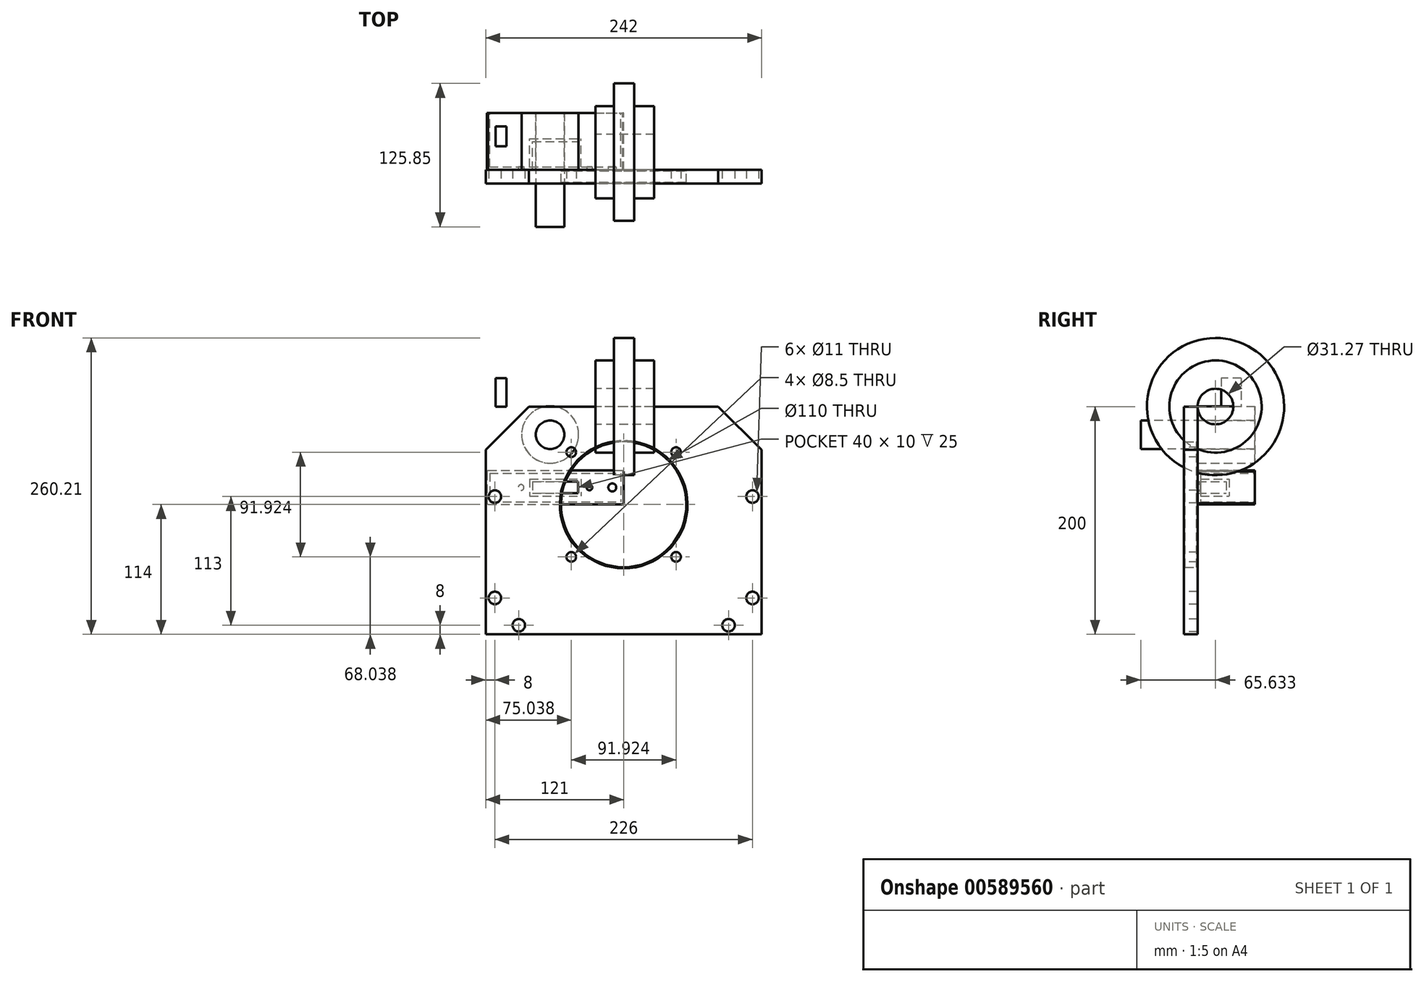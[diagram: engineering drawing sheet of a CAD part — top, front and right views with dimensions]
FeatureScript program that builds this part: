
annotation { "Feature Type Name" : "Feature", "Feature Type Description" : "" }
export const myFeature = defineFeature(function(context is Context, id is Id, definition is map)
    precondition{}
    {
        {
            var Q0;
            Q0=qCreatedBy(makeId("Front.planeOp"),FACE);
            var sketch = newSketch(context, id + "F0", { "sketchPlane" : qUnion([Q0])});
            skLineSegment(sketch, "E0.bottom", {"start": v(-120, 30) * mm, "end": v(0, 30) * mm});
            skLineSegment(sketch, "E0.top", {"start": v(-120, 0) * mm, "end": v(0, 0) * mm});
            skLineSegment(sketch, "E0.left", {"start": v(-120, 30) * mm, "end": v(-120, 0) * mm});
            skLineSegment(sketch, "E0.right", {"start": v(0, 30) * mm, "end": v(0, 0) * mm});
            skSolve(sketch);
        }
        {
            var Q0;
            Q0 = qSketchRegion(id + "F0", true);
            extrude(context, id + "F1", {"entities" : qUnion([Q0]), "depth" : 25 * mm, "offsetDistance" : 25 * mm});
        }
        {
            var Q0;
            Q0=makeQuery(id+"F1.opExtrude","CAP_FACE",FACE,{"disambiguationData":[OSD([sQuery(id+"F0.wireOp",EDGE,"E0.bottom"),sQuery(id+"F0.wireOp",EDGE,"E0.top"),sQuery(id+"F0.wireOp",EDGE,"E0.left"),sQuery(id+"F0.wireOp",EDGE,"E0.right")])],"isStart":false});
            var sketch = newSketch(context, id + "F2", { "sketchPlane" : qUnion([Q0])});
            skLineSegment(sketch, "E1.bottom", {"start": v(-80, 20) * mm, "end": v(-40, 20) * mm});
            skLineSegment(sketch, "E1.top", {"start": v(-80, 10) * mm, "end": v(-40, 10) * mm});
            skLineSegment(sketch, "E1.left", {"start": v(-80, 20) * mm, "end": v(-80, 10) * mm});
            skLineSegment(sketch, "E1.right", {"start": v(-40, 20) * mm, "end": v(-40, 10) * mm});
            skSolve(sketch);
        }
        {
            var Q0;
            Q0=makeQuery(id+"F2.imprint","IMPRINT",FACE,{"disambiguationData":[TD([[makeQuery(id+"F2.imprint","IMPRINT",EDGE,{"derivedFrom":sQuery(id+"F2.wireOp",EDGE,"E1.bottom")}),1.0]])]});
            extrude(context, id + "F3", {"entities" : qUnion([Q0]), "operationType" : NewBodyOperationType.ADD, "depth" : 25 * mm, "offsetDistance" : 25 * mm});
        }
        {
            var Q0;
            Q0=makeQuery(id+"F1.opExtrude","CAP_FACE",FACE,{"disambiguationData":[OSD([sQuery(id+"F0.wireOp",EDGE,"E0.bottom"),sQuery(id+"F0.wireOp",EDGE,"E0.top"),sQuery(id+"F0.wireOp",EDGE,"E0.left"),sQuery(id+"F0.wireOp",EDGE,"E0.right")])],"isStart":true});
            shell(context, id + "F4", {"entities" : qUnion([Q0]), "thickness" : 2.5 * mm});
        }
        {
            var Q0;
            Q0=makeQuery(id+"F3.opExtrude","CAP_FACE",FACE,{"disambiguationData":[OSD([sQuery(id+"F0.wireOp",EDGE,"E0.bottom"),sQuery(id+"F0.wireOp",EDGE,"E0.top"),sQuery(id+"F0.wireOp",EDGE,"E0.left"),sQuery(id+"F0.wireOp",EDGE,"E0.right"),sQuery(id+"F2.wireOp",EDGE,"E1.bottom"),sQuery(id+"F2.wireOp",EDGE,"E1.top"),sQuery(id+"F2.wireOp",EDGE,"E1.left"),sQuery(id+"F2.wireOp",EDGE,"E1.right")])],"isStart":false});
            var sketch = newSketch(context, id + "F5", { "sketchPlane" : qUnion([Q0])});
            skPoint(sketch, "E2", {"position": v(-90, 15) * mm});
            skPoint(sketch, "E3", {"position": v(-30, 15) * mm});
            skPoint(sketch, "E4", {"position": v(-10, 15) * mm});
            skSolve(sketch);
        }
        {
            var Q0;
            Q0=sQuery(id+"F5.wireOp",VERTEX,"E2");
            var Q1;
            Q1=sQuery(id+"F5.wireOp",VERTEX,"E3");
            var Q2;
            Q2=makeQuery(id+"F1.opExtrude","SWEPT_BODY",BODY,{"disambiguationData":[OSD([sQuery(id+"F0.wireOp",EDGE,"E0.bottom"),sQuery(id+"F0.wireOp",EDGE,"E0.top"),sQuery(id+"F0.wireOp",EDGE,"E0.left"),sQuery(id+"F0.wireOp",EDGE,"E0.right")])]});
            hole(context, id + "F6", {"style" : HoleStyle.SIMPLE, "endStyle" : HoleEndStyle.THROUGH, "holeDiameter" : 5 * mm, "majorDiameter" : 5 * mm, "isTappedThrough" : true, "tappedDepth" : 12 * mm, "tapClearance" : 3, "locations" : qUnion([Q0, Q1]), "scope" : qUnion([Q2])});
        }
        {
            var Q0;
            Q0=sQuery(id+"F5.wireOp",VERTEX,"E4");
            var Q1;
            Q1=makeQuery(id+"F1.opExtrude","SWEPT_BODY",BODY,{"disambiguationData":[OSD([sQuery(id+"F0.wireOp",EDGE,"E0.bottom"),sQuery(id+"F0.wireOp",EDGE,"E0.top"),sQuery(id+"F0.wireOp",EDGE,"E0.left"),sQuery(id+"F0.wireOp",EDGE,"E0.right")])]});
            hole(context, id + "F7", {"style" : HoleStyle.SIMPLE, "endStyle" : HoleEndStyle.THROUGH, "standardTappedOrClearance" : lookupTablePath({ "standard" : "ISO", "engagement" : "75%", "pitch" : "1 mm", "size" : "M8", "type" : "Tapped" }), "standardBlindInLast" : lookupTablePath({ "standard" : "ISO", "engagement" : "75%", "pitch" : "1 mm", "size" : "M8", "type" : "Tapped" }), "holeDiameter" : 7 * mm, "majorDiameter" : 8 * mm, "showTappedDepth" : true, "isTappedThrough" : true, "tappedDepth" : 12 * mm, "tapClearance" : 3, "locations" : qUnion([Q0]), "scope" : qUnion([Q1])});
        }
        {
            var Q0;
            {var subQ0=sQuery(id+"F0.wireOp",EDGE,"E0.left");var subQ1=sQuery(id+"F0.wireOp",EDGE,"E0.bottom");Q0=makeQuery(id+"F3.boolean.opBoolean","MERGE",EDGE,{"derivedFrom":[makeQuery(id+"F1.opExtrude","SWEPT_EDGE",EDGE,{"disambiguationData":[OSD([subQ1,subQ0])]}),makeQuery(id+"F3.opExtrude","SWEPT_EDGE",EDGE,{"disambiguationData":[OSD([subQ1,subQ0])]})]});}
            var Q1;
            {var subQ0=sQuery(id+"F0.wireOp",EDGE,"E0.left");var subQ1=sQuery(id+"F0.wireOp",EDGE,"E0.top");Q1=makeQuery(id+"F3.boolean.opBoolean","MERGE",EDGE,{"derivedFrom":[makeQuery(id+"F1.opExtrude","SWEPT_EDGE",EDGE,{"disambiguationData":[OSD([subQ1,subQ0])]}),makeQuery(id+"F3.opExtrude","SWEPT_EDGE",EDGE,{"disambiguationData":[OSD([subQ1,subQ0])]})]});}
            var Q2;
            {var subQ0=sQuery(id+"F0.wireOp",EDGE,"E0.right");var subQ1=sQuery(id+"F0.wireOp",EDGE,"E0.bottom");Q2=makeQuery(id+"F3.boolean.opBoolean","MERGE",EDGE,{"derivedFrom":[makeQuery(id+"F1.opExtrude","SWEPT_EDGE",EDGE,{"disambiguationData":[OSD([subQ1,subQ0])]}),makeQuery(id+"F3.opExtrude","SWEPT_EDGE",EDGE,{"disambiguationData":[OSD([subQ1,subQ0])]})]});}
            var Q3;
            {var subQ0=sQuery(id+"F0.wireOp",EDGE,"E0.right");var subQ1=sQuery(id+"F0.wireOp",EDGE,"E0.top");Q3=makeQuery(id+"F3.boolean.opBoolean","MERGE",EDGE,{"derivedFrom":[makeQuery(id+"F1.opExtrude","SWEPT_EDGE",EDGE,{"disambiguationData":[OSD([subQ1,subQ0])]}),makeQuery(id+"F3.opExtrude","SWEPT_EDGE",EDGE,{"disambiguationData":[OSD([subQ1,subQ0])]})]});}
            chamfer(context, id + "F8", {"entities" : qUnion([Q0, Q1, Q2, Q3]), "width" : 1 * mm, "tangentPropagation" : true});
        }
        {
            var Q0;
            Q0=qCreatedBy(makeId("Front.planeOp"),FACE);
            var sketch = newSketch(context, id + "F9", { "sketchPlane" : qUnion([Q0])});
            skCircle(sketch, "E5", {"center": v(-64.52, 61.3) * mm, "radius": 25 * mm});
            skCircle(sketch, "E6", {"center": v(-64.52, 61.3) * mm, "radius": 12.5 * mm});
            skSolve(sketch);
        }
        {
            var Q0;
            Q0=makeQuery(id+"F9.imprint","IMPRINT",FACE,{"disambiguationData":[TD([[makeQuery(id+"F9.imprint","IMPRINT",EDGE,{"derivedFrom":sQuery(id+"F9.wireOp",EDGE,"E5")}),1.0]])]});
            extrude(context, id + "F10", {"entities" : qUnion([Q0]), "depth" : 50 * mm, "offsetDistance" : 25 * mm});
        }
        {
            var Q0;
            Q0=makeQuery(id+"F10.opExtrude","CAP_FACE",FACE,{"disambiguationData":[OSD([sQuery(id+"F9.wireOp",EDGE,"E5"),sQuery(id+"F9.wireOp",EDGE,"E6")])],"isStart":false});
            var sketch = newSketch(context, id + "F11", { "sketchPlane" : qUnion([Q0])});
            skCircle(sketch, "E7", {"center": v(-64.52, 61.3) * mm, "radius": 12.54 * mm});
            skSolve(sketch);
        }
        {
            var Q0;
            Q0=qCreatedBy(makeId("Front.planeOp"),FACE);
            cPlane(context, id + "F12", {"entities" : qUnion([Q0]), "cplaneType" : CPlaneType.OFFSET, "offset" : 50 * mm, "width" : 150 * mm, "height" : 150 * mm});
        }
        {
            var Q0;
            Q0=qCreatedBy(id+"F12.planeOp",FACE);
            var sketch = newSketch(context, id + "F13", { "sketchPlane" : qUnion([Q0])});
            skCircle(sketch, "E8.0", {"center": v(-64.52, 61.3) * mm, "radius": 12.54 * mm});
            skSolve(sketch);
        }
        {
            var Q0;
            Q0 = qSketchRegion(id + "F13", true);
            extrude(context, id + "F14", {"entities" : qUnion([Q0]), "oppositeDirection" : true, "depth" : 50 * mm, "offsetDistance" : 25 * mm, "hasSecondDirection" : true, "secondDirectionOppositeDirection" : false, "secondDirectionDepth" : 50 * mm});
        }
        {
            var Q0;
            Q0=qCreatedBy(id+"F12.planeOp",FACE);
            var sketch = newSketch(context, id + "F15", { "sketchPlane" : qUnion([Q0])});
            skLineSegment(sketch, "E9.bottom", {"start": v(121, 86) * mm, "end": v(-121, 86) * mm});
            skLineSegment(sketch, "E9.top", {"start": v(121, -114) * mm, "end": v(-121, -114) * mm});
            skLineSegment(sketch, "E9.left", {"start": v(121, 86) * mm, "end": v(121, -114) * mm});
            skLineSegment(sketch, "E9.right", {"start": v(-121, 86) * mm, "end": v(-121, -114) * mm});
            skPoint(sketch, "E9.middle", {"position": v(0, -14) * mm});
            skCircle(sketch, "E10", {"center": v(0, 0) * mm, "radius": 55 * mm});
            skSolve(sketch);
        }
        {
            var Q0;
            Q0=makeQuery(id+"F15.imprint","IMPRINT",FACE,{"disambiguationData":[TD([[makeQuery(id+"F15.imprint","IMPRINT",EDGE,{"derivedFrom":sQuery(id+"F15.wireOp",EDGE,"E9.bottom")}),1.0]])]});
            extrude(context, id + "F16", {"entities" : qUnion([Q0]), "depth" : 12 * mm, "offsetDistance" : 25 * mm});
        }
        {
            var Q0;
            Q0=makeQuery(id+"F16.opExtrude","SWEPT_EDGE",EDGE,{"disambiguationData":[OSD([sQuery(id+"F15.wireOp",EDGE,"E9.bottom"),sQuery(id+"F15.wireOp",EDGE,"E9.right")])]});
            var Q1;
            Q1=makeQuery(id+"F16.opExtrude","SWEPT_EDGE",EDGE,{"disambiguationData":[OSD([sQuery(id+"F15.wireOp",EDGE,"E9.bottom"),sQuery(id+"F15.wireOp",EDGE,"E9.left")])]});
            chamfer(context, id + "F17", {"entities" : qUnion([Q0, Q1]), "width" : 38 * mm, "tangentPropagation" : true});
        }
        {
            var Q0;
            Q0=makeQuery(id+"F16.opExtrude","CAP_FACE",FACE,{"disambiguationData":[OSD([sQuery(id+"F15.wireOp",EDGE,"E9.bottom"),sQuery(id+"F15.wireOp",EDGE,"E9.top"),sQuery(id+"F15.wireOp",EDGE,"E9.left"),sQuery(id+"F15.wireOp",EDGE,"E9.right"),sQuery(id+"F15.wireOp",EDGE,"E10")])],"isStart":false});
            var sketch = newSketch(context, id + "F18", { "sketchPlane" : qUnion([Q0])});
            skCircle(sketch, "E11", {"center": v(0, 0) * mm, "radius": 65 * mm, "construction": true});
            skPoint(sketch, "E12", {"position": v(45.96, 45.96) * mm});
            skPoint(sketch, "E13", {"position": v(45.96, -45.96) * mm});
            skPoint(sketch, "E14", {"position": v(-45.96, -45.96) * mm});
            skPoint(sketch, "E15", {"position": v(-45.96, 45.96) * mm});
            skLineSegment(sketch, "E16", {"start": v(-45.96, -45.96) * mm, "end": v(45.96, 45.96) * mm, "construction": true});
            skLineSegment(sketch, "E17", {"start": v(-45.96, 45.96) * mm, "end": v(45.96, -45.96) * mm, "construction": true});
            skSolve(sketch);
        }
        {
            var Q0;
            Q0=sQuery(id+"F18.wireOp",VERTEX,"E15");
            var Q1;
            Q1=sQuery(id+"F18.wireOp",VERTEX,"E12");
            var Q2;
            Q2=sQuery(id+"F18.wireOp",VERTEX,"E13");
            var Q3;
            Q3=sQuery(id+"F18.wireOp",VERTEX,"E14");
            var Q4;
            Q4=makeQuery(id+"F16.opExtrude","SWEPT_BODY",BODY,{"disambiguationData":[OSD([sQuery(id+"F15.wireOp",EDGE,"E9.bottom"),sQuery(id+"F15.wireOp",EDGE,"E9.top"),sQuery(id+"F15.wireOp",EDGE,"E9.left"),sQuery(id+"F15.wireOp",EDGE,"E9.right"),sQuery(id+"F15.wireOp",EDGE,"E10")])]});
            hole(context, id + "F19", {"style" : HoleStyle.SIMPLE, "endStyle" : HoleEndStyle.THROUGH, "standardTappedOrClearance" : lookupTablePath({ "standard" : "ISO", "engagement" : "75%", "pitch" : "1.5 mm", "size" : "M10", "type" : "Tapped" }), "standardBlindInLast" : lookupTablePath({ "standard" : "ISO", "engagement" : "75%", "pitch" : "1.5 mm", "size" : "M10", "type" : "Tapped" }), "holeDiameter" : 8.5 * mm, "majorDiameter" : 10 * mm, "showTappedDepth" : true, "isTappedThrough" : true, "tappedDepth" : 12 * mm, "tapClearance" : 3, "locations" : qUnion([Q0, Q1, Q2, Q3]), "scope" : qUnion([Q4])});
        }
        {
            var Q0;
            Q0=makeQuery(id+"F16.opExtrude","CAP_FACE",FACE,{"disambiguationData":[OSD([sQuery(id+"F15.wireOp",EDGE,"E9.bottom"),sQuery(id+"F15.wireOp",EDGE,"E9.top"),sQuery(id+"F15.wireOp",EDGE,"E9.left"),sQuery(id+"F15.wireOp",EDGE,"E9.right"),sQuery(id+"F15.wireOp",EDGE,"E10")])],"isStart":false});
            var sketch = newSketch(context, id + "F20", { "sketchPlane" : qUnion([Q0])});
            skLineSegment(sketch, "E18.bottom", {"start": v(-113, 7) * mm, "end": v(113, 7) * mm});
            skLineSegment(sketch, "E18.top", {"start": v(-113, -106) * mm, "end": v(113, -106) * mm});
            skLineSegment(sketch, "E18.left", {"start": v(-113, 7) * mm, "end": v(-113, -106) * mm});
            skLineSegment(sketch, "E18.right", {"start": v(113, 7) * mm, "end": v(113, -106) * mm});
            skPoint(sketch, "E19", {"position": v(-113, 7) * mm});
            skPoint(sketch, "E20", {"position": v(113, 7) * mm});
            skPoint(sketch, "E21", {"position": v(-113, -82) * mm});
            skPoint(sketch, "E22", {"position": v(113, -82) * mm});
            skPoint(sketch, "E23", {"position": v(-92, -106) * mm});
            skPoint(sketch, "E24", {"position": v(92, -106) * mm});
            skSolve(sketch);
        }
        {
            var Q0;
            Q0=sQuery(id+"F20.wireOp",VERTEX,"E19");
            var Q1;
            Q1=sQuery(id+"F20.wireOp",VERTEX,"E20");
            var Q2;
            Q2=sQuery(id+"F20.wireOp",VERTEX,"E22");
            var Q3;
            Q3=sQuery(id+"F20.wireOp",VERTEX,"E24");
            var Q4;
            Q4=sQuery(id+"F20.wireOp",VERTEX,"E23");
            var Q5;
            Q5=sQuery(id+"F20.wireOp",VERTEX,"E21");
            var Q6;
            Q6=makeQuery(id+"F16.opExtrude","SWEPT_BODY",BODY,{"disambiguationData":[OSD([sQuery(id+"F15.wireOp",EDGE,"E9.bottom"),sQuery(id+"F15.wireOp",EDGE,"E9.top"),sQuery(id+"F15.wireOp",EDGE,"E9.left"),sQuery(id+"F15.wireOp",EDGE,"E9.right"),sQuery(id+"F15.wireOp",EDGE,"E10")])]});
            hole(context, id + "F21", {"style" : HoleStyle.SIMPLE, "endStyle" : HoleEndStyle.THROUGH, "standardTappedOrClearance" : lookupTablePath({ "standard" : "ISO", "fit" : "Normal", "size" : "M10", "type" : "Clearance" }), "standardBlindInLast" : lookupTablePath({ "fit" : "Standard", "standard" : "ISO", "size" : "M10", "type" : "Clearance" }), "holeDiameter" : 11 * mm, "majorDiameter" : 10 * mm, "isTappedThrough" : true, "tappedDepth" : 12 * mm, "tapClearance" : 3, "locations" : qUnion([Q0, Q1, Q2, Q3, Q4, Q5]), "scope" : qUnion([Q6])});
        }
        {
            var Q0;
            Q0=makeQuery(id+"F16.opExtrude","CAP_EDGE",EDGE,{"disambiguationData":[OSD([sQuery(id+"F15.wireOp",EDGE,"E10")])],"isStart":false});
            var Q1;
            Q1=makeQuery(id+"F16.opExtrude","CAP_EDGE",EDGE,{"disambiguationData":[OSD([sQuery(id+"F15.wireOp",EDGE,"E10")])],"isStart":true});
            chamfer(context, id + "F22", {"entities" : qUnion([Q0, Q1]), "width" : 1 * mm, "tangentPropagation" : true});
        }
        {
            var Q0;
            Q0=makeQuery(id+"F16.opExtrude","SWEPT_FACE",FACE,{"disambiguationData":[OSD([sQuery(id+"F15.wireOp",EDGE,"E9.bottom")])]});
            var sketch = newSketch(context, id + "F23", { "sketchPlane" : qUnion([Q0])});
            skLineSegment(sketch, "E25.bottom", {"start": v(-112.36, -11.81) * mm, "end": v(-102.75, -11.81) * mm});
            skLineSegment(sketch, "E25.top", {"start": v(-112.36, -29.22) * mm, "end": v(-102.75, -29.22) * mm});
            skLineSegment(sketch, "E25.left", {"start": v(-112.36, -11.81) * mm, "end": v(-112.36, -29.22) * mm});
            skLineSegment(sketch, "E25.right", {"start": v(-102.75, -11.81) * mm, "end": v(-102.75, -29.22) * mm});
            skSolve(sketch);
        }
        {
            var Q0;
            Q0=makeQuery(id+"F23.imprint","IMPRINT",FACE,{"disambiguationData":[TD([[makeQuery(id+"F23.imprint","IMPRINT",EDGE,{"derivedFrom":sQuery(id+"F23.wireOp",EDGE,"E25.bottom")}),-1.0]])]});
            extrude(context, id + "F24", {"entities" : qUnion([Q0]), "operationType" : NewBodyOperationType.ADD, "depth" : 25 * mm, "offsetDistance" : 25 * mm});
        }
        {
            var Q0;
            Q0=makeQuery(id+"F16.opExtrude","SWEPT_FACE",FACE,{"disambiguationData":[OSD([sQuery(id+"F15.wireOp",EDGE,"E9.bottom")])]});
            var sketch = newSketch(context, id + "F25", { "sketchPlane" : qUnion([Q0])});
            skLineSegment(sketch, "E26.bottom", {"start": v(-24.62, -50) * mm, "end": v(26.77, -50) * mm});
            skLineSegment(sketch, "E26.top", {"start": v(-24.62, -74.83) * mm, "end": v(-8.44, -74.83) * mm});
            skLineSegment(sketch, "E26.left", {"start": v(-24.62, -50) * mm, "end": v(-24.62, -74.83) * mm});
            skLineSegment(sketch, "E26.right", {"start": v(26.77, -50) * mm, "end": v(26.77, -74.83) * mm});
            skLineSegment(sketch, "E27", {"start": v(-8.44, -74.83) * mm, "end": v(-8.44, -94.58) * mm});
            skLineSegment(sketch, "E28", {"start": v(-8.44, -94.58) * mm, "end": v(9.17, -94.58) * mm});
            skLineSegment(sketch, "E29", {"start": v(9.17, -94.58) * mm, "end": v(9.17, -74.83) * mm});
            skLineSegment(sketch, "E30.trimOffspring", {"start": v(9.17, -74.83) * mm, "end": v(26.77, -74.83) * mm});
            skLineSegment(sketch, "E31", {"start": v(-50.25, -34.37) * mm, "end": v(52.35, -34.37) * mm, "construction": true});
            skSolve(sketch);
        }
        {
            var Q0;
            Q0 = qSketchRegion(id + "F25", true);
            var Q1;
            Q1=sQuery(id+"F25.wireOp",EDGE,"E31");
            revolve(context, id + "F26", {"entities" : qUnion([Q0]), "axis" : qUnion([Q1]), "revolveType" : RevolveType.FULL});
        }
    });
